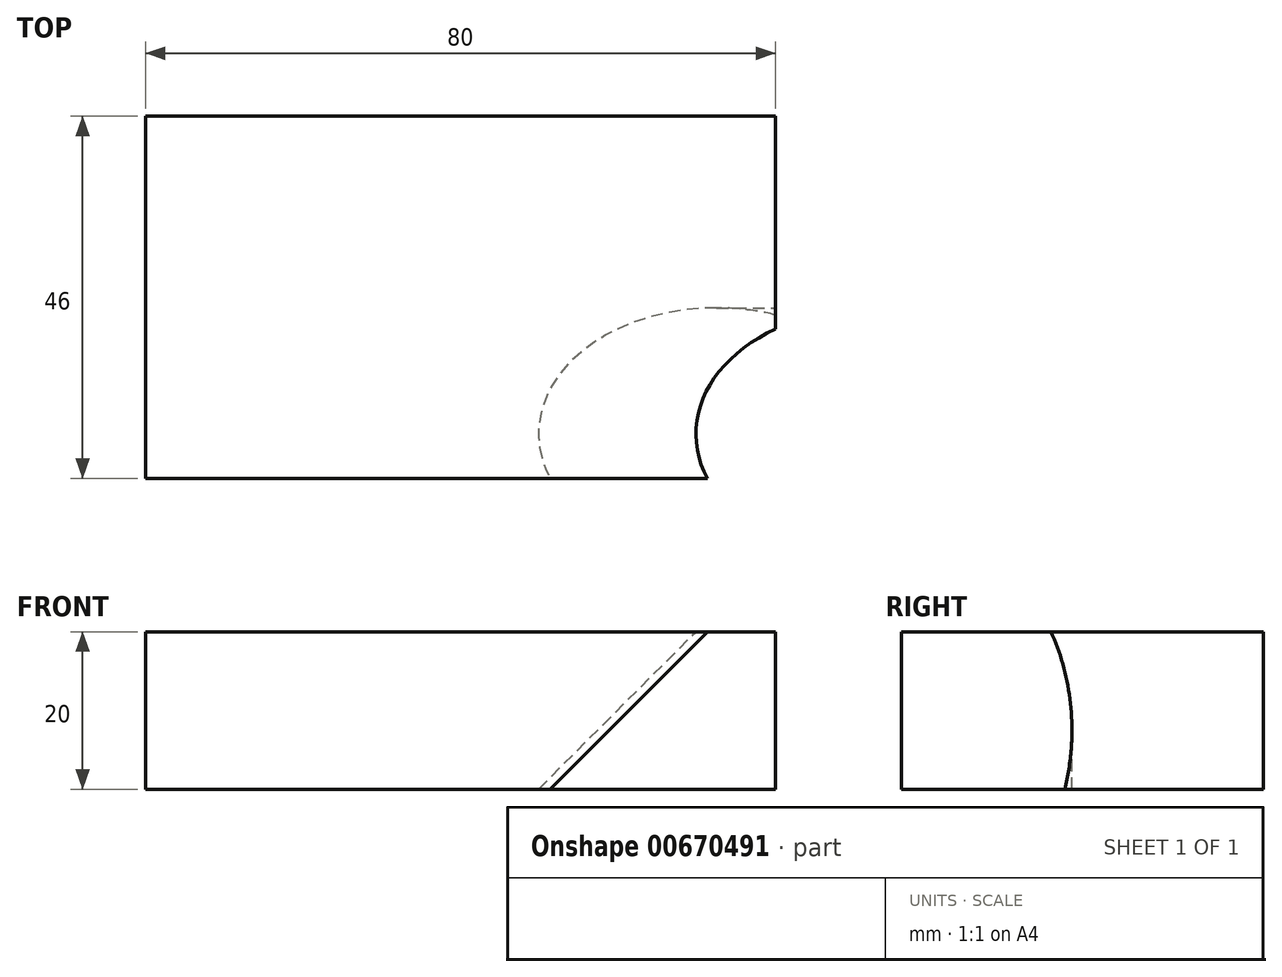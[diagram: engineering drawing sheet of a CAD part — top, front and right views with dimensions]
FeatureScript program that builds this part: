
annotation { "Feature Type Name" : "Feature", "Feature Type Description" : "" }
export const myFeature = defineFeature(function(context is Context, id is Id, definition is map)
    precondition{}
    {
        {
            var Q0;
            Q0=qCreatedBy(makeId("Top.planeOp"),FACE);
            var sketch = newSketch(context, id + "F0", { "sketchPlane" : qUnion([Q0])});
            skLineSegment(sketch, "E0.bottom", {"start": v(-40, 46) * mm, "end": v(40, 46) * mm});
            skLineSegment(sketch, "E0.top", {"start": v(-40, 0) * mm, "end": v(40, 0) * mm});
            skLineSegment(sketch, "E0.left", {"start": v(-40, 46) * mm, "end": v(-40, 0) * mm});
            skLineSegment(sketch, "E0.right", {"start": v(40, 46) * mm, "end": v(40, 0) * mm});
            skLineSegment(sketch, "E1", {"start": v(0, 0) * mm, "end": v(0, 79.69) * mm, "construction": true});
            skSolve(sketch);
        }
        {
            var Q0;
            Q0=makeQuery(id+"F0.imprint","IMPRINT",FACE,{"disambiguationData":[TD([[makeQuery(id+"F0.imprint","IMPRINT",EDGE,{"derivedFrom":sQuery(id+"F0.wireOp",EDGE,"E0.bottom")}),-1.0]])]});
            extrude(context, id + "F1", {"entities" : qUnion([Q0]), "depth" : 20 * mm, "offsetDistance" : 25 * mm});
        }
        {
            var Q0;
            Q0=makeQuery(id+"F1.opExtrude","CAP_FACE",FACE,{"disambiguationData":[OSD([sQuery(id+"F0.wireOp",EDGE,"E0.bottom"),sQuery(id+"F0.wireOp",EDGE,"E0.top"),sQuery(id+"F0.wireOp",EDGE,"E0.left"),sQuery(id+"F0.wireOp",EDGE,"E0.right")])],"isStart":false});
            var sketch = newSketch(context, id + "F2", { "sketchPlane" : qUnion([Q0])});
            skPoint(sketch, "E2", {"position": v(12, 23) * mm});
            skSolve(sketch);
        }
        {
            var Q0;
            Q0=makeQuery(id+"F2.imprint","IMPRINT",FACE,{"disambiguationData":[TD([[makeQuery(id+"F2.imprint","IMPRINT",EDGE,{"derivedFrom":makeQuery(id+"F1.opExtrude","CAP_EDGE",EDGE,{"disambiguationData":[OSD([sQuery(id+"F0.wireOp",EDGE,"E0.bottom")])],"isStart":false})}),-1.0]])]});
            var Q1;
            Q1=makeQuery(id+"F1.opExtrude","CAP_EDGE",EDGE,{"disambiguationData":[OSD([sQuery(id+"F0.wireOp",EDGE,"E0.right")])],"isStart":false});
            cPlane(context, id + "F3", {"entities" : qUnion([Q0, Q1]), "cplaneType" : CPlaneType.LINE_ANGLE, "offset" : 25 * mm, "angle" : 45 * degree, "oppositeDirection" : true, "width" : 150 * mm, "height" : 150 * mm});
        }
        {
            var Q0;
            Q0=qCreatedBy(id+"F3.planeOp",FACE);
            var sketch = newSketch(context, id + "F4", { "sketchPlane" : qUnion([Q0])});
            skCircle(sketch, "E3", {"center": v(-5.66, -23) * mm, "radius": 16 * mm});
            skSolve(sketch);
        }
        {
            var Q0;
            Q0=makeQuery(id+"F4.imprint","IMPRINT",FACE,{"disambiguationData":[TD([[makeQuery(id+"F4.imprint","IMPRINT",EDGE,{"derivedFrom":sQuery(id+"F4.wireOp",EDGE,"E3")}),1.0]])]});
            extrude(context, id + "F5", {"entities" : qUnion([Q0]), "operationType" : NewBodyOperationType.REMOVE, "endBound" : BoundingType.THROUGH_ALL, "depth" : 25 * mm, "offsetDistance" : 25 * mm});
        }
    });
